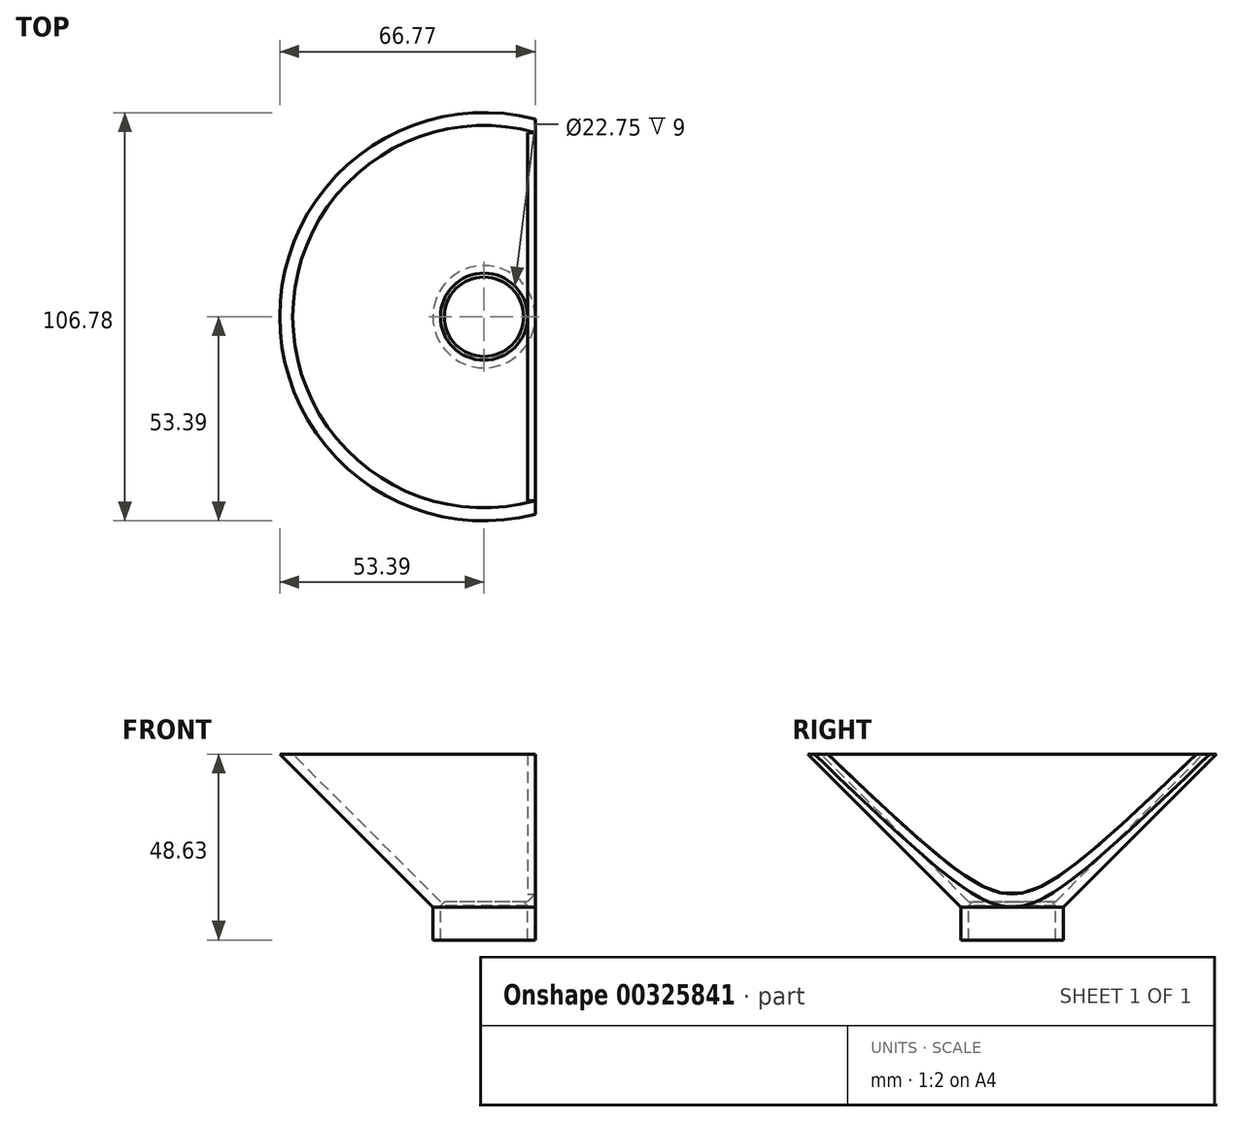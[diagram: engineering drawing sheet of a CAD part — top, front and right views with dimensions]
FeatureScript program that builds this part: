
annotation { "Feature Type Name" : "Feature", "Feature Type Description" : "" }
export const myFeature = defineFeature(function(context is Context, id is Id, definition is map)
    precondition{}
    {
        {
            var Q0;
            Q0=qCreatedBy(makeId("Front.planeOp"),FACE);
            var sketch = newSketch(context, id + "F0", { "sketchPlane" : qUnion([Q0])});
            skLineSegment(sketch, "E0", {"start": v(50, 40.02) * mm, "end": v(11.38, 1.4) * mm});
            skLineSegment(sketch, "E1", {"start": v(11.38, 1.4) * mm, "end": v(11.38, -8.6) * mm});
            skLineSegment(sketch, "E2", {"start": v(11.38, -8.6) * mm, "end": v(13.37, -8.6) * mm});
            skLineSegment(sketch, "E3", {"start": v(13.37, -8.6) * mm, "end": v(13.37, 0) * mm});
            skLineSegment(sketch, "E4", {"start": v(13.38, 0) * mm, "end": v(53.4, 40.02) * mm});
            skLineSegment(sketch, "E5", {"start": v(53.4, 40.02) * mm, "end": v(50, 40.02) * mm});
            skLineSegment(sketch, "E6", {"start": v(0, 47.16) * mm, "end": v(0, -26.85) * mm, "construction": true});
            skLineSegment(sketch, "E7", {"start": v(11.38, 1.4) * mm, "end": v(10.37, 1.4) * mm});
            skLineSegment(sketch, "E8", {"start": v(10.37, 1.4) * mm, "end": v(11.38, 0.4) * mm});
            skLineSegment(sketch, "E9", {"start": v(13.37, -8.6) * mm, "end": v(23.37, -8.6) * mm});
            skLineSegment(sketch, "E10", {"start": v(23.37, -8.6) * mm, "end": v(23.37, 0) * mm});
            skLineSegment(sketch, "E11", {"start": v(23.37, 0) * mm, "end": v(63.4, 40.02) * mm});
            skPoint(sketch, "E11.endSnap0", {"position": v(51.7, 40.02) * mm});
            skLineSegment(sketch, "E12", {"start": v(63.4, 40.02) * mm, "end": v(53.4, 40.02) * mm});
            skSolve(sketch);
        }
        {
            var Q0;
            Q0=makeQuery(id+"F0.imprint","IMPRINT",FACE,{"disambiguationData":[TD([[makeQuery(id+"F0.imprint","IMPRINT",EDGE,{"derivedFrom":sQuery(id+"F0.wireOp",EDGE,"E0")}),1.0]])]});
            var Q1;
            {var subQ0=sQuery(id+"F0.wireOp",EDGE,"E7");Q1=makeQuery(id+"F0.imprint","IMPRINT",FACE,{"disambiguationData":[TD([[makeQuery(id+"F0.imprint","IMPRINT",EDGE,{"derivedFrom":subQ0}),1.0]])]});}
            var Q2;
            Q2=sQuery(id+"F0.wireOp",EDGE,"E6");
            revolve(context, id + "F1", {"entities" : qUnion([Q0, Q1]), "axis" : qUnion([Q2]), "revolveType" : RevolveType.FULL});
        }
        {
            var Q0;
            Q0=qCreatedBy(makeId("Top.planeOp"),FACE);
            var sketch = newSketch(context, id + "F2", { "sketchPlane" : qUnion([Q0])});
            skCircle(sketch, "E13.0", {"center": v(0, 0) * mm, "radius": 53.4 * mm});
            skCircle(sketch, "E14.0", {"center": v(0, 0) * mm, "radius": 11.38 * mm});
            skLineSegment(sketch, "E15", {"start": v(13.37, 51.7) * mm, "end": v(13.38, -51.7) * mm});
            skLineSegment(sketch, "E16", {"start": v(13.38, 51.7) * mm, "end": v(53.4, 51.7) * mm});
            skLineSegment(sketch, "E17", {"start": v(53.4, 51.7) * mm, "end": v(53.4, -51.7) * mm});
            skLineSegment(sketch, "E18", {"start": v(53.4, -51.7) * mm, "end": v(13.38, -51.7) * mm});
            skCircle(sketch, "E19.0", {"center": v(0, 0) * mm, "radius": 13.37 * mm});
            skSolve(sketch);
        }
        {
            var Q0;
            {var subQ0=sQuery(id+"F2.wireOp",EDGE,"E16");Q0=makeQuery(id+"F2.imprint","IMPRINT",FACE,{"disambiguationData":[TD([[makeQuery(id+"F2.imprint","IMPRINT",EDGE,{"derivedFrom":subQ0}),-1.0]])]});}
            var Q1;
            {var subQ1=sQuery(id+"F2.wireOp",EDGE,"E13.0");var subQ3=makeQuery(id+"F2.imprint","INTERSECT",VERTEX,{"derivedFrom":[subQ1,sQuery(id+"F2.wireOp",EDGE,"E17")]});Q1=makeQuery(id+"F2.imprint","IMPRINT",FACE,{"disambiguationData":[TD([[makeQuery(id+"F2.imprint","IMPRINT",EDGE,{"disambiguationData":[TD([[subQ3,-1.0]])],"derivedFrom":subQ1}),1.0]])]});}
            var Q2;
            {var subQ1=sQuery(id+"F2.wireOp",EDGE,"E13.0");var subQ3=makeQuery(id+"F2.imprint","INTERSECT",VERTEX,{"derivedFrom":[subQ1,sQuery(id+"F2.wireOp",EDGE,"E17")]});Q2=makeQuery(id+"F2.imprint","IMPRINT",FACE,{"disambiguationData":[TD([[makeQuery(id+"F2.imprint","IMPRINT",EDGE,{"disambiguationData":[TD([[subQ3,-1.0]])],"derivedFrom":subQ1}),1.0]])]});}
            var Q3;
            {var subQ0=sQuery(id+"F2.wireOp",EDGE,"E18");Q3=makeQuery(id+"F2.imprint","IMPRINT",FACE,{"disambiguationData":[TD([[makeQuery(id+"F2.imprint","IMPRINT",EDGE,{"derivedFrom":subQ0}),-1.0]])]});}
            extrude(context, id + "F3", {"entities" : qUnion([Q0, Q1, Q2, Q3]), "operationType" : NewBodyOperationType.REMOVE, "endBound" : BoundingType.THROUGH_ALL, "depth" : 25 * mm});
        }
        {
            var Q0;
            Q0=makeQuery(id+"F3.boolean.opBoolean","COPY",FACE,{"derivedFrom":makeQuery(id+"F3.opExtrude","SWEPT_FACE",FACE,{"disambiguationData":[OSD([sQuery(id+"F2.wireOp",EDGE,"E15")])]})});
            var sketch = newSketch(context, id + "F4", { "sketchPlane" : qUnion([Q0])});
            skFitSpline(sketch, "E20.0", {"points": [v(-162.54, 149.7) * mm, v(-154.74, 141.94) * mm, v(-143.05, 130.3) * mm, v(-127.45, 114.77) * mm, v(-115.74, 103.14) * mm, v(-104.03, 91.5) * mm, v(-92.3, 79.89) * mm, v(-80.57, 68.29) * mm, v(-70.77, 58.64) * mm, v(-62.9, 50.93) * mm, v(-57, 45.17) * mm, v(-51.08, 39.42) * mm, v(-45.14, 33.7) * mm, v(-39.17, 28) * mm, v(-33.15, 22.35) * mm, v(-28.07, 17.7) * mm, v(-23.95, 14.05) * mm, v(-20.82, 11.36) * mm, v(-17.63, 8.73) * mm, v(-14.37, 6.21) * mm, v(-11.55, 4.25) * mm, v(-9.19, 2.83) * mm, v(-7.36, 1.86) * mm, v(-5.78, 1.17) * mm, v(-4.48, 0.72) * mm, v(-3.49, 0.44) * mm, v(-2.47, 0.21) * mm, v(-1.11, 0.02) * mm, v(0.26, -0.03) * mm, v(1.64, 0.09) * mm, v(3, 0.3) * mm, v(4.66, 0.75) * mm, v(6.6, 1.5) * mm, v(8.44, 2.42) * mm, v(10.22, 3.44) * mm, v(12.51, 4.9) * mm, v(15.28, 6.9) * mm, v(18.51, 9.44) * mm, v(21.66, 12.06) * mm, v(24.76, 14.75) * mm, v(28.83, 18.39) * mm, v(33.86, 23) * mm, v(39.82, 28.62) * mm, v(45.75, 34.28) * mm, v(51.64, 39.96) * mm, v(57.52, 45.67) * mm, v(63.38, 51.4) * mm, v(71.18, 59.05) * mm, v(80.91, 68.63) * mm, v(92.57, 80.15) * mm, v(104.2, 91.68) * mm, v(115.83, 103.23) * mm, v(127.46, 114.78) * mm, v(139.07, 126.34) * mm, v(154.55, 141.75) * mm, v(173.9, 161.03) * mm, v(197.1, 184.18) * mm, v(212.57, 199.61) * mm, v(220.3, 207.33) * mm]});
            skFitSpline(sketch, "E21.0", {"points": [v(-162.54, 149.7) * mm, v(-154.74, 141.94) * mm, v(-143.05, 130.3) * mm, v(-127.45, 114.77) * mm, v(-115.74, 103.14) * mm, v(-104.03, 91.5) * mm, v(-92.3, 79.89) * mm, v(-80.57, 68.29) * mm, v(-70.77, 58.64) * mm, v(-62.9, 50.93) * mm, v(-57, 45.17) * mm, v(-51.08, 39.42) * mm, v(-45.14, 33.7) * mm, v(-39.17, 28) * mm, v(-33.15, 22.35) * mm, v(-28.07, 17.7) * mm, v(-23.95, 14.05) * mm, v(-20.82, 11.36) * mm, v(-17.63, 8.73) * mm, v(-14.37, 6.21) * mm, v(-11.55, 4.25) * mm, v(-9.19, 2.83) * mm, v(-7.36, 1.86) * mm, v(-5.78, 1.17) * mm, v(-4.48, 0.72) * mm, v(-3.49, 0.44) * mm, v(-2.47, 0.21) * mm, v(-1.11, 0.02) * mm, v(0.26, -0.03) * mm, v(1.64, 0.09) * mm, v(3, 0.3) * mm, v(4.66, 0.75) * mm, v(6.6, 1.5) * mm, v(8.44, 2.42) * mm, v(10.22, 3.44) * mm, v(12.51, 4.9) * mm, v(15.28, 6.9) * mm, v(18.51, 9.44) * mm, v(21.66, 12.06) * mm, v(24.76, 14.75) * mm, v(28.83, 18.39) * mm, v(33.86, 23) * mm, v(39.82, 28.62) * mm, v(45.75, 34.28) * mm, v(51.64, 39.96) * mm, v(57.52, 45.67) * mm, v(63.38, 51.4) * mm, v(71.18, 59.05) * mm, v(80.91, 68.63) * mm, v(92.57, 80.15) * mm, v(104.2, 91.68) * mm, v(115.83, 103.23) * mm, v(127.46, 114.78) * mm, v(139.07, 126.34) * mm, v(154.55, 141.75) * mm, v(173.9, 161.03) * mm, v(197.1, 184.18) * mm, v(212.57, 199.61) * mm, v(220.3, 207.33) * mm]});
            skLineSegment(sketch, "E22.0", {"start": v(-50, 40.02) * mm, "end": v(50, 40.02) * mm});
            skLineSegment(sketch, "E23.0", {"start": v(-48.18, 40.02) * mm, "end": v(-51.7, 40.02) * mm});
            skLineSegment(sketch, "E24.0", {"start": v(51.7, 40.02) * mm, "end": v(48.18, 40.02) * mm});
            skSolve(sketch);
        }
        {
            var Q0;
            {var subQ10=sQuery(id+"F4.wireOp",EDGE,"E21.0");Q0=makeQuery(id+"F4.imprint","IMPRINT",FACE,{"disambiguationData":[TD([[makeQuery(id+"F4.imprint","IMPRINT",EDGE,{"derivedFrom":subQ10}),1.0]])]});}
            var Q1;
            Q1=makeQuery(id+"F4.imprint","IMPRINT",FACE,{"disambiguationData":[TD([[makeQuery(id+"F4.imprint","IMPRINT",EDGE,{"derivedFrom":sQuery(id+"F4.wireOp",EDGE,"E22.0")}),-1.0]])]});
            extrude(context, id + "F5", {"entities" : qUnion([Q0, Q1]), "operationType" : NewBodyOperationType.ADD, "oppositeDirection" : true, "depth" : 2 * mm});
        }
    });
